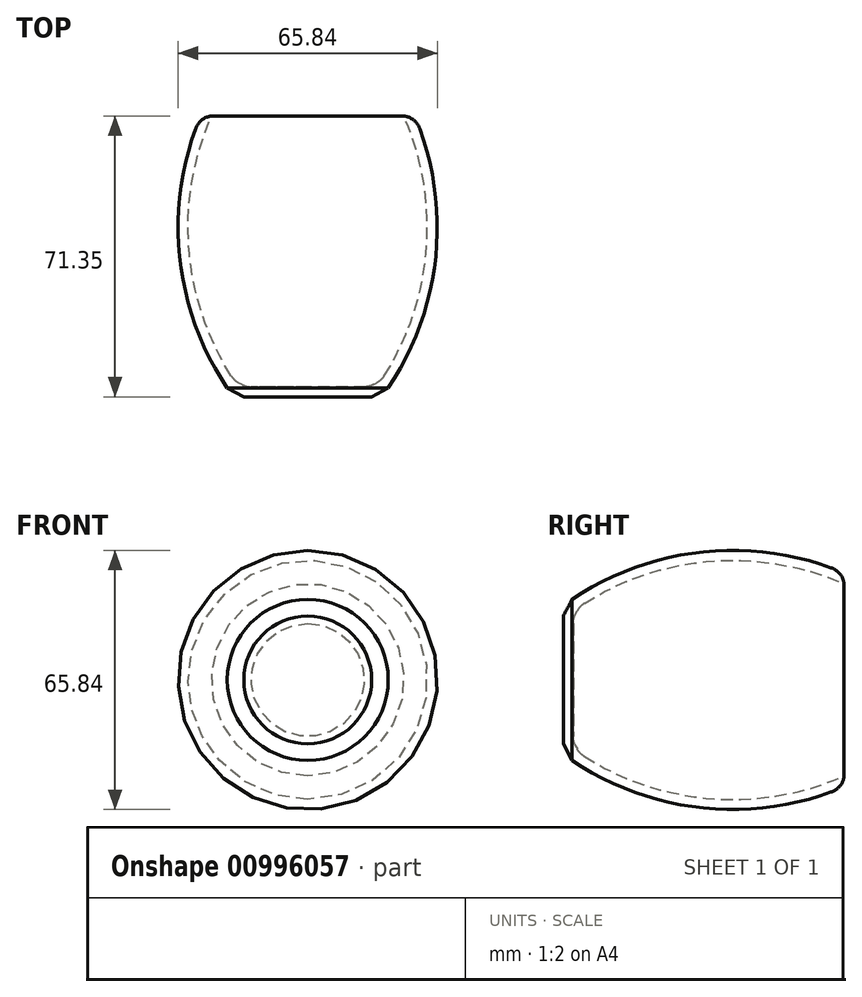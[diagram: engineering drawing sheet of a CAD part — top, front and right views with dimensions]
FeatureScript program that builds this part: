
annotation { "Feature Type Name" : "Feature", "Feature Type Description" : "" }
export const myFeature = defineFeature(function(context is Context, id is Id, definition is map)
    precondition{}
    {
        {
            var Q0;
            Q0=qCreatedBy(makeId("Top.planeOp"),FACE);
            var sketch = newSketch(context, id + "F0", { "sketchPlane" : qUnion([Q0])});
            skLineSegment(sketch, "E0", {"start": v(0, 39.83) * mm, "end": v(27.19, 39.83) * mm});
            skArc(sketch, "E1", {"start": v(18.88, -31.52) * mm, "mid": v(32.43, 3.06) * mm, "end": v(27.19, 39.83) * mm});
            skLineSegment(sketch, "E2", {"start": v(18.88, -31.52) * mm, "end": v(0, -31.52) * mm});
            skLineSegment(sketch, "E3", {"start": v(0, -31.52) * mm, "end": v(0, 39.83) * mm});
            skSolve(sketch);
        }
        {
            var Q0;
            Q0=makeQuery(id+"F0.imprint","IMPRINT",FACE,{"disambiguationData":[TD([[makeQuery(id+"F0.imprint","IMPRINT",EDGE,{"derivedFrom":sQuery(id+"F0.wireOp",EDGE,"E0")}),-1.0]])]});
            var Q1;
            Q1=sQuery(id+"F0.wireOp",EDGE,"E3");
            revolve(context, id + "F1", {"surfaceOperationType" : NewSurfaceOperationType.NEW, "entities" : qUnion([Q0]), "axis" : qUnion([Q1]), "revolveType" : RevolveType.FULL});
        }
        {
            var Q0;
            Q0=makeQuery(id+"F1.opRevolve","SWEPT_EDGE",EDGE,{"disambiguationData":[OSD([sQuery(id+"F0.wireOp",EDGE,"E1"),sQuery(id+"F0.wireOp",EDGE,"E2")])]});
            chamfer(context, id + "F2", {"entities" : qUnion([Q0]), "width" : 5.08 * mm, "tangentPropagation" : true});
        }
        {
            var Q0;
            Q0=makeQuery(id+"F1.opRevolve","SWEPT_FACE",FACE,{"disambiguationData":[OSD([sQuery(id+"F0.wireOp",EDGE,"E0")])]});
            shell(context, id + "F3", {"entities" : qUnion([Q0]), "thickness" : 2.54 * mm});
        }
        {
            var Q0;
            Q0=makeQuery(id+"F1.opRevolve","SWEPT_EDGE",EDGE,{"disambiguationData":[OSD([sQuery(id+"F0.wireOp",EDGE,"E0"),sQuery(id+"F0.wireOp",EDGE,"E1")])]});
            var Q1;
            {var subQ0=sQuery(id+"F0.wireOp",EDGE,"E2");var subQ1=sQuery(id+"F0.wireOp",EDGE,"E1");Q1=makeQuery(id+"F3.opShell","OFFSET_EDGE",EDGE,{"disambiguationData":[OSD([subQ1,subQ0]),TDD([makeQuery(id+"F2.opChamfer","BLEND_EDGE",EDGE,{"blendedFrom":[makeQuery(id+"F1.opRevolve","SWEPT_EDGE",EDGE,{"disambiguationData":[OSD([subQ1,subQ0])]}),makeQuery(id+"F1.opRevolve","SWEPT_FACE",FACE,{"disambiguationData":[OSD([subQ0])]})],"blendedInto":[makeQuery(id+"F1.opRevolve","SWEPT_FACE",FACE,{"disambiguationData":[OSD([subQ0])]})]})])]});}
            var Q2;
            {var subQ0=sQuery(id+"F0.wireOp",EDGE,"E1");var subQ1=sQuery(id+"F0.wireOp",EDGE,"E2");Q2=makeQuery(id+"F3.opShell","OFFSET_EDGE",EDGE,{"disambiguationData":[OSD([subQ0,subQ1]),TDD([makeQuery(id+"F2.opChamfer","BLEND_EDGE",EDGE,{"blendedFrom":[makeQuery(id+"F1.opRevolve","SWEPT_EDGE",EDGE,{"disambiguationData":[OSD([subQ0,subQ1])]}),makeQuery(id+"F1.opRevolve","SWEPT_FACE",FACE,{"disambiguationData":[OSD([subQ0])]})],"blendedInto":[makeQuery(id+"F1.opRevolve","SWEPT_FACE",FACE,{"disambiguationData":[OSD([subQ0])]})]})])]});}
            fillet(context, id + "F4", {"entities" : qUnion([Q0, Q1, Q2]), "radius" : 5.08 * mm, "rho" : 0.5, "crossSection" : FilletCrossSection.CONIC, "allowEdgeOverflow" : false});
        }
    });
